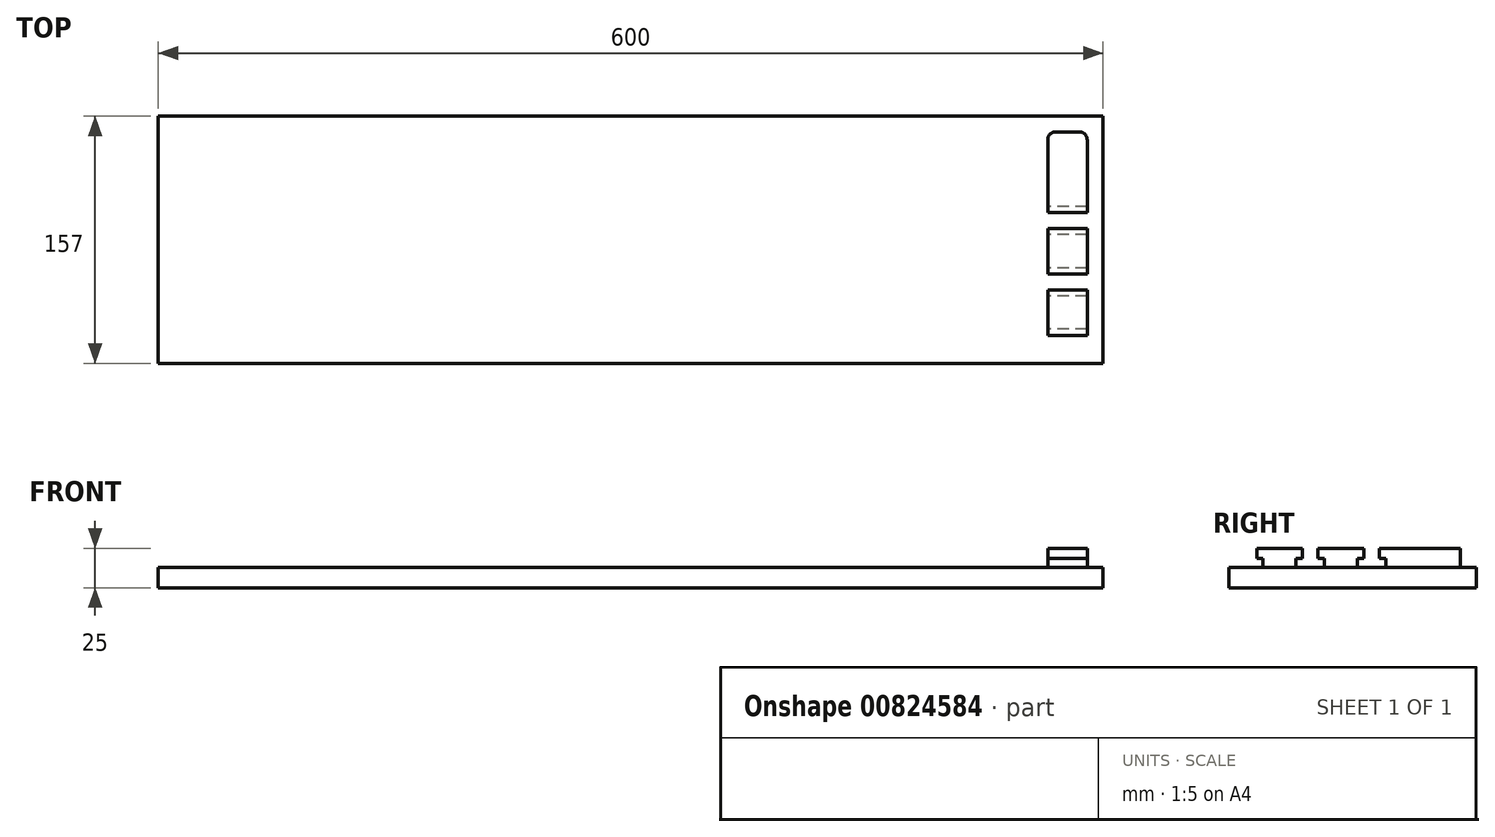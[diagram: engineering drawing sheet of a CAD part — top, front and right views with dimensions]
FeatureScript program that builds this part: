
annotation { "Feature Type Name" : "Feature", "Feature Type Description" : "" }
export const myFeature = defineFeature(function(context is Context, id is Id, definition is map)
    precondition{}
    {
        {
            var Q0;
            Q0=qCreatedBy(makeId("Top.planeOp"),FACE);
            var sketch = newSketch(context, id + "F0", { "sketchPlane" : qUnion([Q0])});
            skLineSegment(sketch, "E0.bottom", {"start": v(-300, -55.34) * mm, "end": v(300, -55.34) * mm});
            skLineSegment(sketch, "E0.top", {"start": v(-300, 101.66) * mm, "end": v(300, 101.66) * mm});
            skLineSegment(sketch, "E0.left", {"start": v(-300, -55.34) * mm, "end": v(-300, 101.66) * mm});
            skLineSegment(sketch, "E0.right", {"start": v(300, -55.34) * mm, "end": v(300, 101.66) * mm});
            skSolve(sketch);
        }
        {
            var Q0;
            Q0=qSketchRegion(id+"F0",true);
            extrude(context, id + "F1", {"entities" : qUnion([Q0]), "depth" : 25 * mm});
        }
        {
            var Q0;
            Q0=makeQuery(id+"F1.opExtrude","CAP_FACE",FACE,{"disambiguationData":[OSD([sQuery(id+"F0.wireOp",EDGE,"E0.bottom"),sQuery(id+"F0.wireOp",EDGE,"E0.top"),sQuery(id+"F0.wireOp",EDGE,"E0.left"),sQuery(id+"F0.wireOp",EDGE,"E0.right")])],"isStart":false});
            var sketch = newSketch(context, id + "F2", { "sketchPlane" : qUnion([Q0])});
            skLineSegment(sketch, "E1.bottom", {"start": v(-285, 91.66) * mm, "end": v(-270, 91.66) * mm});
            skLineSegment(sketch, "E1.top", {"start": v(-285, -45.34) * mm, "end": v(-270, -45.34) * mm});
            skLineSegment(sketch, "E1.left", {"start": v(-290, 86.66) * mm, "end": v(-290, -40.34) * mm});
            skLineSegment(sketch, "E1.right", {"start": v(-265, 86.66) * mm, "end": v(-265, -40.34) * mm});
            skPoint(sketch, "E2.visualSharp", {"position": v(-290, 91.66) * mm});
            skArc(sketch, "E2.filletArc", {"start": v(-285, 91.66) * mm, "mid": v(-288.54, 90.2) * mm, "end": v(-290, 86.66) * mm});
            skPoint(sketch, "E3.visualSharp", {"position": v(-265, 91.66) * mm});
            skArc(sketch, "E3.filletArc", {"start": v(-265, 86.66) * mm, "mid": v(-266.46, 90.2) * mm, "end": v(-270, 91.66) * mm});
            skPoint(sketch, "E4.visualSharp", {"position": v(-265, -45.34) * mm});
            skArc(sketch, "E4.filletArc", {"start": v(-270, -45.34) * mm, "mid": v(-266.46, -43.87) * mm, "end": v(-265, -40.34) * mm});
            skPoint(sketch, "E5.visualSharp", {"position": v(-290, -45.34) * mm});
            skArc(sketch, "E5.filletArc", {"start": v(-290, -40.34) * mm, "mid": v(-288.54, -43.87) * mm, "end": v(-285, -45.34) * mm});
            skArc(sketch, "E6.MirrorCS", {"start": v(290, -40.34) * mm, "mid": v(288.54, -43.87) * mm, "end": v(285, -45.34) * mm});
            skArc(sketch, "E7.MirrorCS", {"start": v(285, 91.66) * mm, "mid": v(288.54, 90.2) * mm, "end": v(290, 86.66) * mm});
            skArc(sketch, "E8.MirrorCS", {"start": v(265, 86.66) * mm, "mid": v(266.46, 90.2) * mm, "end": v(270, 91.66) * mm});
            skArc(sketch, "E9.MirrorCS", {"start": v(270, -45.34) * mm, "mid": v(266.46, -43.87) * mm, "end": v(265, -40.34) * mm});
            skPoint(sketch, "E10.MirrorP", {"position": v(290, 91.66) * mm});
            skLineSegment(sketch, "E11.MirrorCS", {"start": v(265, 86.66) * mm, "end": v(265, -40.34) * mm});
            skLineSegment(sketch, "E12.MirrorCS", {"start": v(290, 86.66) * mm, "end": v(290, -40.34) * mm});
            skLineSegment(sketch, "E13.MirrorCS", {"start": v(285, 91.66) * mm, "end": v(270, 91.66) * mm});
            skLineSegment(sketch, "E14.MirrorCS", {"start": v(285, -45.34) * mm, "end": v(270, -45.34) * mm});
            skPoint(sketch, "E15.MirrorP", {"position": v(290, -45.34) * mm});
            skPoint(sketch, "E16.MirrorP", {"position": v(265, -45.34) * mm});
            skPoint(sketch, "E17.MirrorP", {"position": v(265, 91.66) * mm});
            skSolve(sketch);
        }
        {
            var Q0;
            Q0=makeQuery(id+"F2.imprint","IMPRINT",FACE,{"disambiguationData":[TD([[makeQuery(id+"F2.imprint","IMPRINT",EDGE,{"derivedFrom":sQuery(id+"F2.wireOp",EDGE,"E1.bottom")}),-1.0]])]});
            var Q1;
            Q1=makeQuery(id+"F2.imprint","IMPRINT",FACE,{"disambiguationData":[TD([[makeQuery(id+"F2.imprint","IMPRINT",EDGE,{"derivedFrom":sQuery(id+"F2.wireOp",EDGE,"E6.MirrorCS")}),-1.0]])]});
            extrude(context, id + "F3", {"entities" : qUnion([Q0, Q1]), "operationType" : NewBodyOperationType.REMOVE, "oppositeDirection" : true, "depth" : 12 * mm});
        }
        {
            var Q0;
            Q0=makeQuery(id+"F3.boolean.opBoolean","COPY",FACE,{"derivedFrom":makeQuery(id+"F3.opExtrude","SWEPT_FACE",FACE,{"disambiguationData":[OSD([sQuery(id+"F2.wireOp",EDGE,"E11.MirrorCS")])]})});
            var sketch = newSketch(context, id + "F4", { "sketchPlane" : qUnion([Q0])});
            skLineSegment(sketch, "E18", {"start": v(-40.34, 25) * mm, "end": v(-40.34, 18.5) * mm});
            skLineSegment(sketch, "E19", {"start": v(-40.34, 18.5) * mm, "end": v(-44.34, 18.5) * mm});
            skLineSegment(sketch, "E20", {"start": v(-44.34, 18.5) * mm, "end": v(-44.34, 13) * mm});
            skLineSegment(sketch, "E21", {"start": v(-44.34, 13) * mm, "end": v(-26.34, 13) * mm});
            skLineSegment(sketch, "E22", {"start": v(-26.34, 13) * mm, "end": v(-26.34, 18.5) * mm});
            skLineSegment(sketch, "E23", {"start": v(-26.34, 18.5) * mm, "end": v(-30.34, 18.5) * mm});
            skLineSegment(sketch, "E24", {"start": v(-30.34, 18.5) * mm, "end": v(-30.34, 25) * mm});
            skLineSegment(sketch, "E25", {"start": v(-40.34, 25) * mm, "end": v(-30.34, 25) * mm});
            skLineSegment(sketch, "E26.1.0.0", {"start": v(-1.34, 18.5) * mm, "end": v(-5.34, 18.5) * mm});
            skLineSegment(sketch, "E26.1.0.1", {"start": v(-1.34, 25) * mm, "end": v(-1.34, 18.5) * mm});
            skLineSegment(sketch, "E26.1.0.2", {"start": v(-5.34, 18.5) * mm, "end": v(-5.34, 13) * mm});
            skLineSegment(sketch, "E26.1.0.3", {"start": v(-5.34, 13) * mm, "end": v(12.66, 13) * mm});
            skLineSegment(sketch, "E26.1.0.4", {"start": v(12.66, 13) * mm, "end": v(12.66, 18.5) * mm});
            skLineSegment(sketch, "E26.1.0.5", {"start": v(12.66, 18.5) * mm, "end": v(8.66, 18.5) * mm});
            skLineSegment(sketch, "E26.1.0.6", {"start": v(-1.34, 25) * mm, "end": v(8.66, 25) * mm});
            skLineSegment(sketch, "E26.1.0.7", {"start": v(8.66, 18.5) * mm, "end": v(8.66, 25) * mm});
            skLineSegment(sketch, "E26.2.0.0", {"start": v(37.66, 18.5) * mm, "end": v(33.66, 18.5) * mm});
            skLineSegment(sketch, "E26.2.0.1", {"start": v(37.66, 25) * mm, "end": v(37.66, 18.5) * mm});
            skLineSegment(sketch, "E26.2.0.2", {"start": v(33.66, 18.5) * mm, "end": v(33.66, 13) * mm});
            skLineSegment(sketch, "E26.2.0.3", {"start": v(33.66, 13) * mm, "end": v(51.66, 13) * mm});
            skLineSegment(sketch, "E26.2.0.4", {"start": v(51.66, 13) * mm, "end": v(51.66, 18.5) * mm});
            skLineSegment(sketch, "E26.2.0.5", {"start": v(51.66, 18.5) * mm, "end": v(47.66, 18.5) * mm});
            skLineSegment(sketch, "E26.2.0.6", {"start": v(37.66, 25) * mm, "end": v(47.66, 25) * mm});
            skLineSegment(sketch, "E26.2.0.7", {"start": v(47.66, 18.5) * mm, "end": v(47.66, 25) * mm});
            skLineSegment(sketch, "E26.3.0.0", {"start": v(76.66, 18.5) * mm, "end": v(72.66, 18.5) * mm});
            skLineSegment(sketch, "E26.3.0.1", {"start": v(76.66, 25) * mm, "end": v(76.66, 18.5) * mm});
            skLineSegment(sketch, "E26.3.0.2", {"start": v(72.66, 18.5) * mm, "end": v(72.66, 13) * mm});
            skLineSegment(sketch, "E26.3.0.3", {"start": v(72.66, 13) * mm, "end": v(90.66, 13) * mm});
            skLineSegment(sketch, "E26.3.0.4", {"start": v(90.66, 13) * mm, "end": v(90.66, 18.5) * mm});
            skLineSegment(sketch, "E26.3.0.5", {"start": v(90.66, 18.5) * mm, "end": v(86.66, 18.5) * mm});
            skLineSegment(sketch, "E26.3.0.6", {"start": v(76.66, 25) * mm, "end": v(86.66, 25) * mm});
            skLineSegment(sketch, "E26.3.0.7", {"start": v(86.66, 18.5) * mm, "end": v(86.66, 25) * mm});
            skLineSegment(sketch, "E26.direction1", {"start": v(-44.34, 13) * mm, "end": v(-5.34, 13) * mm, "construction": true});
            skSolve(sketch);
        }
        {
            var Q0;
            Q0=qSketchRegion(id+"F4",true);
            extrude(context, id + "F5", {"entities" : qUnion([Q0]), "operationType" : NewBodyOperationType.REMOVE, "oppositeDirection" : true, "depth" : 545 * mm});
        }
        {
            var Q0;
            Q0=qSketchRegion(id+"F4",true);
            extrude(context, id + "F6", {"entities" : qUnion([Q0]), "operationType" : NewBodyOperationType.REMOVE, "depth" : 16 * mm});
        }
    });
